# Revit family: BE_24308_de_DE
name_source: partatom
category: Leuchten
revit_build: Autodesk Revit 2015 (Build: 20160512_0715(x64)
units: mm (PartAtom-declared; Revit-internal decimal feet)

## types (4) — shared parameters
AC/DC = AC/DC
Aktualisierung = 2017-07-26T04:09:29
BEGA_Dummy = Nein
BEGA_IES = Ja
BEGA_Intern = Ja
BEGA_Intern_Konstruktion = Ja
BEGA_Intern_an = Ja
BEGA_Intern_aus = Ja
Beschreibung = Deckeneinbau-Tiefstrahler
Beschreibung_Sonderanfertigung = Hier können Sie Informationen zur Sonderanfertigung eintragen.
Bestellnummer_Einbaugehäuse = ---
CE_Konformität = ja
Einbaugehäuse = Nein
Einbautiefe = 100 mm
Einbauöffnung = 1527 x 70 mm
Energieeffizienzklasse = LED A++ - A
Farbfilter = 16777215
Farbtemperaturverschiebung bei Dämpfen der Lampe = <Keine Auswahl>
Farbwiedergabeindex = Ra > 80
Frequenz = 0/50-60 Hz
Gewicht = 6.45 kg
Hersteller = BEGA
Lampe = LED 48 W
Lastklassifizierung = Beleuchtung
Lebensdauerkriterien = L70B50 @ 25 °C = 198000 h
Logo = BEGA_Logo.png
M_G = Nein
Material_02 = BEGA_Oberfläche_Silber_matt
Material_03 = BEGA_Oberfläche_Weiss_matt
Material_05 = BEGA_Oberfläche_Aluminium Guss
Material_06 = BEGA_Oberfläche_Edelstahl_gebürstet
Material_09 = BEGA_Glas_klar
Material_11 = BEGA_Glas_opal
Material_15 = BEGA_Leuchtmedium_matt
Material_17 = BEGA_Reflektor
Neigungswinkel = 0.00°
Produktdatenblatt = http://www.bega.de
Scheinlast = 0 VA
Schutzart = IP 65
Schutzklasse = I
Sonderanfertigung = Nein
Spannung = 240 V
Typenbild = 24308.png
URL = http://www.bega.de
Umgebungstemperatur = 25 °C
zero-valued in all types: Vorgabe-Ansicht

## per-type parameters (varying)
| type | Bestellnummer | Datei für fotometrisches Netz | Farbtemperatur | LED_Modulbezeichnung | Lampenlichtstrom | Leuchtenlichtstrom | M_A | M_W | Modell |
| BEGA_24308_Silber_K4 | 24308AK4 | BE_24308K4.IES | 4000 K | LED-0771/840 | 8580 lm | 6253 lm | Ja | Nein | 24308AK4 |
| BEGA_24308_Silber_K3 | 24308A | BE_24308.IES | 3000 K | LED-0771/830 | 8370 lm | 6100 lm | Ja | Nein | 24308A |
| BEGA_24308_Weiß_K3 | 24308 | BE_24308.IES | 3000 K | LED-0771/830 | 8370 lm | 6100 lm | Nein | Ja | 24308 |
| BEGA_24308_Weiß_K4 | 24308K4 | BE_24308K4.IES | 4000 K | LED-0771/840 | 8580 lm | 6253 lm | Nein | Ja | 24308K4 |
